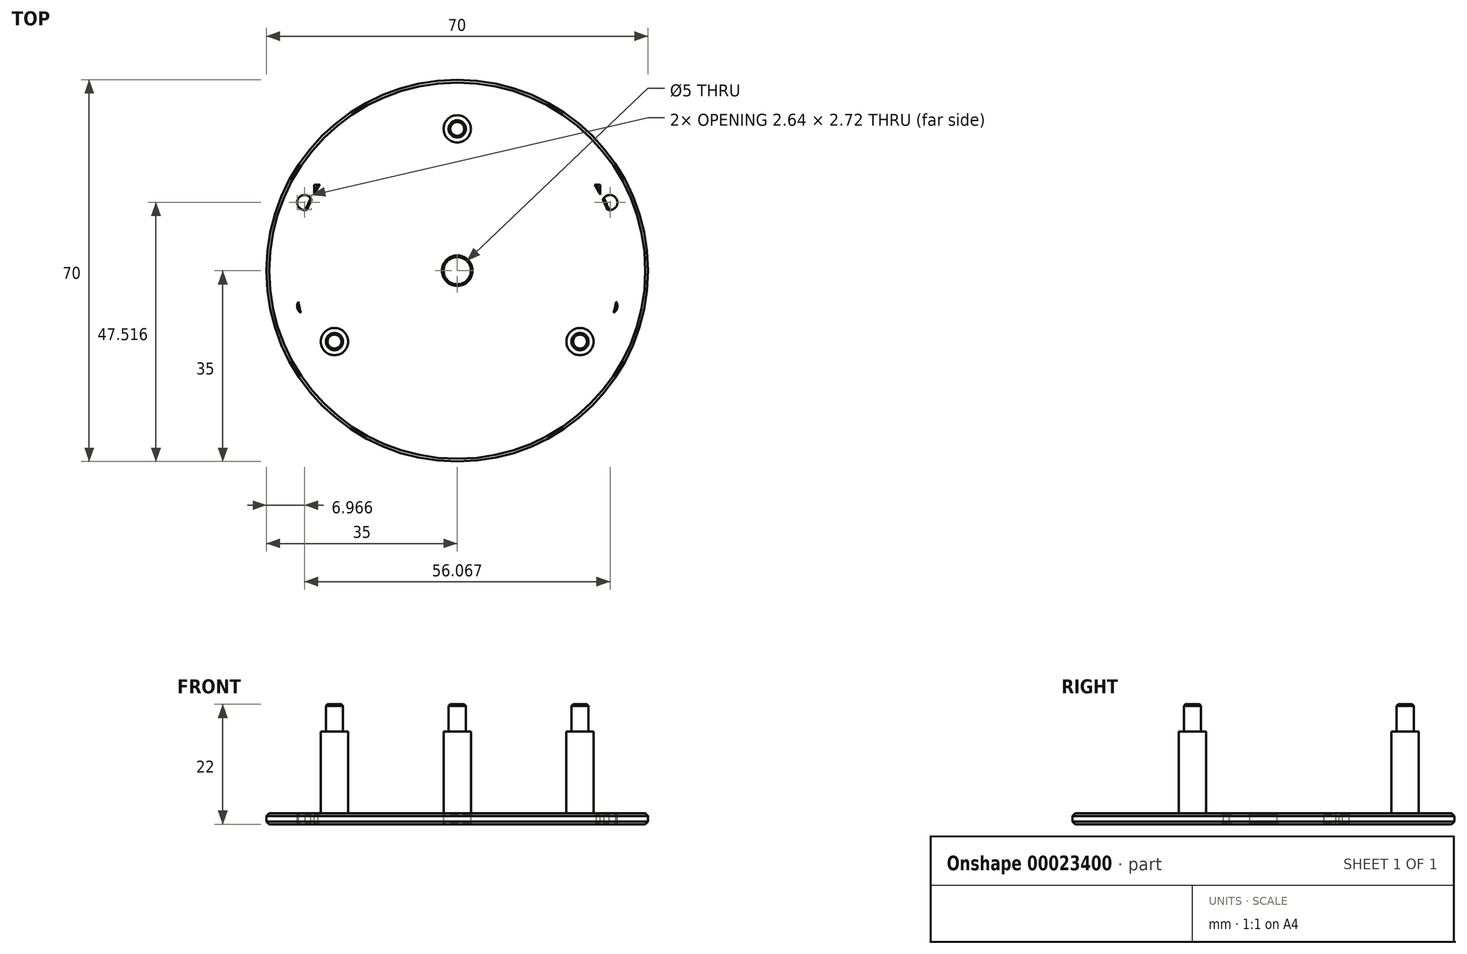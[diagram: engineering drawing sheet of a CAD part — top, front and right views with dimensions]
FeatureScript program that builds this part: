
annotation { "Feature Type Name" : "Feature", "Feature Type Description" : "" }
export const myFeature = defineFeature(function(context is Context, id is Id, definition is map)
    precondition{}
    {
        {
            var Q0;
            Q0=qCreatedBy(makeId("Top.planeOp"),FACE);
            var sketch = newSketch(context, id + "F0", { "sketchPlane" : qUnion([Q0])});
            skCircle(sketch, "E0", {"center": v(0, 0) * mm, "radius": 35 * mm});
            skCircle(sketch, "E1", {"center": v(0, 0) * mm, "radius": 30 * mm, "construction": true});
            skCircle(sketch, "E2.cCircle", {"center": v(0, 0) * mm, "radius": 26 * mm, "construction": true});
            skLineSegment(sketch, "E2.0", {"start": v(0, 26) * mm, "end": v(22.52, -13) * mm, "construction": true});
            skLineSegment(sketch, "E2.1", {"start": v(22.52, -13) * mm, "end": v(-22.52, -13) * mm, "construction": true});
            skLineSegment(sketch, "E2.2", {"start": v(-22.52, -13) * mm, "end": v(0, 26) * mm, "construction": true});
            skCircle(sketch, "E3", {"center": v(0, 26) * mm, "radius": 1.57 * mm});
            skCircle(sketch, "E4", {"center": v(22.52, -13) * mm, "radius": 1.57 * mm});
            skCircle(sketch, "E5", {"center": v(-22.52, -13) * mm, "radius": 1.57 * mm});
            skSolve(sketch);
        }
        {
            var Q0;
            Q0=makeQuery(id+"F0.imprint","IMPRINT",FACE,{"disambiguationData":[TD([[makeQuery(id+"F0.imprint","IMPRINT",EDGE,{"derivedFrom":sQuery(id+"F0.wireOp",EDGE,"E0")}),1.0]])]});
            extrude(context, id + "F1", {"entities" : qUnion([Q0]), "oppositeDirection" : true, "depth" : 2 * mm});
        }
        {
            var Q0;
            Q0=makeQuery(id+"F1.opExtrude","CAP_FACE",FACE,{"disambiguationData":[OSD([sQuery(id+"F0.wireOp",EDGE,"E0"),sQuery(id+"F0.wireOp",EDGE,"E3"),sQuery(id+"F0.wireOp",EDGE,"E4"),sQuery(id+"F0.wireOp",EDGE,"E5")])],"isStart":true});
            var sketch = newSketch(context, id + "F2", { "sketchPlane" : qUnion([Q0])});
            skLineSegment(sketch, "E6.bottom", {"start": v(-31.25, 15.75) * mm, "end": v(31.25, 15.75) * mm, "construction": true});
            skLineSegment(sketch, "E6.top", {"start": v(-31.25, -9.75) * mm, "end": v(31.25, -9.75) * mm, "construction": true});
            skLineSegment(sketch, "E6.left", {"start": v(-31.25, 15.75) * mm, "end": v(-31.25, -9.75) * mm, "construction": true});
            skLineSegment(sketch, "E6.right", {"start": v(31.25, 15.75) * mm, "end": v(31.25, -9.75) * mm, "construction": true});
            skCircle(sketch, "E7", {"center": v(-28, 12.5) * mm, "radius": 1.38 * mm});
            skCircle(sketch, "E8", {"center": v(-28, -6.5) * mm, "radius": 1.38 * mm});
            skCircle(sketch, "E9", {"center": v(28, 12.5) * mm, "radius": 1.38 * mm});
            skCircle(sketch, "E10", {"center": v(28, -6.5) * mm, "radius": 1.38 * mm});
            skLineSegment(sketch, "E11.bottom", {"start": v(-26.25, 15.75) * mm, "end": v(26.25, 15.75) * mm});
            skLineSegment(sketch, "E11.top", {"start": v(-26.25, -9.75) * mm, "end": v(26.25, -9.75) * mm});
            skLineSegment(sketch, "E11.left", {"start": v(-26.25, 15.75) * mm, "end": v(-26.25, -9.75) * mm});
            skLineSegment(sketch, "E11.right", {"start": v(26.25, 15.75) * mm, "end": v(26.25, -9.75) * mm});
            skPoint(sketch, "E12.0", {"position": v(-22.52, -13) * mm});
            skLineSegment(sketch, "E13", {"start": v(-26.25, 0) * mm, "end": v(26.25, 0) * mm, "construction": true});
            skPoint(sketch, "E14.0", {"position": v(0, 0) * mm});
            skSolve(sketch);
        }
        {
            var Q0;
            Q0=makeQuery(id+"F2.imprint","IMPRINT",FACE,{"disambiguationData":[TD([[makeQuery(id+"F2.imprint","IMPRINT",EDGE,{"derivedFrom":sQuery(id+"F2.wireOp",EDGE,"E7")}),1.0]])]});
            var Q1;
            Q1=makeQuery(id+"F2.imprint","IMPRINT",FACE,{"disambiguationData":[TD([[makeQuery(id+"F2.imprint","IMPRINT",EDGE,{"derivedFrom":sQuery(id+"F2.wireOp",EDGE,"E11.bottom")}),-1.0]])]});
            var Q2;
            Q2=makeQuery(id+"F2.imprint","IMPRINT",FACE,{"disambiguationData":[TD([[makeQuery(id+"F2.imprint","IMPRINT",EDGE,{"derivedFrom":sQuery(id+"F2.wireOp",EDGE,"E8")}),1.0]])]});
            var Q3;
            Q3=makeQuery(id+"F2.imprint","IMPRINT",FACE,{"disambiguationData":[TD([[makeQuery(id+"F2.imprint","IMPRINT",EDGE,{"derivedFrom":sQuery(id+"F2.wireOp",EDGE,"E9")}),1.0]])]});
            var Q4;
            Q4=makeQuery(id+"F2.imprint","IMPRINT",FACE,{"disambiguationData":[TD([[makeQuery(id+"F2.imprint","IMPRINT",EDGE,{"derivedFrom":sQuery(id+"F2.wireOp",EDGE,"E10")}),1.0]])]});
            extrude(context, id + "F3", {"entities" : qUnion([Q0, Q1, Q2, Q3, Q4]), "operationType" : NewBodyOperationType.REMOVE, "endBound" : BoundingType.UP_TO_NEXT, "oppositeDirection" : true, "depth" : 25 * mm});
        }
        {
            var Q0;
            Q0=makeQuery(id+"F1.opExtrude","CAP_EDGE",EDGE,{"disambiguationData":[OSD([sQuery(id+"F0.wireOp",EDGE,"E0")])],"isStart":true});
            var Q1;
            Q1=makeQuery(id+"F1.opExtrude","CAP_EDGE",EDGE,{"disambiguationData":[OSD([sQuery(id+"F0.wireOp",EDGE,"E3")])],"isStart":true});
            var Q2;
            Q2=makeQuery(id+"F1.opExtrude","CAP_EDGE",EDGE,{"disambiguationData":[OSD([sQuery(id+"F0.wireOp",EDGE,"E5")])],"isStart":true});
            var Q3;
            Q3=makeQuery(id+"F1.opExtrude","CAP_EDGE",EDGE,{"disambiguationData":[OSD([sQuery(id+"F0.wireOp",EDGE,"E4")])],"isStart":true});
            var Q4;
            Q4=makeQuery(id+"F1.opExtrude","CAP_EDGE",EDGE,{"disambiguationData":[OSD([sQuery(id+"F0.wireOp",EDGE,"E0")])],"isStart":false});
            var Q5;
            Q5=makeQuery(id+"F1.opExtrude","CAP_EDGE",EDGE,{"disambiguationData":[OSD([sQuery(id+"F0.wireOp",EDGE,"E4")])],"isStart":false});
            var Q6;
            Q6=makeQuery(id+"F1.opExtrude","CAP_EDGE",EDGE,{"disambiguationData":[OSD([sQuery(id+"F0.wireOp",EDGE,"E3")])],"isStart":false});
            var Q7;
            Q7=makeQuery(id+"F1.opExtrude","CAP_EDGE",EDGE,{"disambiguationData":[OSD([sQuery(id+"F0.wireOp",EDGE,"E5")])],"isStart":false});
            var Q8;
            Q8=makeQuery(id+"F3.boolean.opBoolean","COPY",EDGE,{"derivedFrom":makeQuery(id+"F3.opExtrude","CAP_EDGE",EDGE,{"disambiguationData":[OSD([sQuery(id+"F2.wireOp",EDGE,"E7")])],"isStart":true})});
            var Q9;
            Q9=makeQuery(id+"F3.boolean.opBoolean","COPY",EDGE,{"derivedFrom":makeQuery(id+"F3.opExtrude","CAP_EDGE",EDGE,{"disambiguationData":[OSD([sQuery(id+"F2.wireOp",EDGE,"E8")])],"isStart":true})});
            var Q10;
            Q10=makeQuery(id+"F3.boolean.opBoolean","COPY",EDGE,{"derivedFrom":makeQuery(id+"F3.opExtrude","CAP_EDGE",EDGE,{"disambiguationData":[OSD([sQuery(id+"F2.wireOp",EDGE,"E9")])],"isStart":true})});
            var Q11;
            Q11=makeQuery(id+"F3.boolean.opBoolean","COPY",EDGE,{"derivedFrom":makeQuery(id+"F3.opExtrude","CAP_EDGE",EDGE,{"disambiguationData":[OSD([sQuery(id+"F2.wireOp",EDGE,"E10")])],"isStart":true})});
            var Q12;
            Q12=makeQuery(id+"F3.boolean.opBoolean","COPY",EDGE,{"derivedFrom":makeQuery(id+"F3.opExtrude","CAP_EDGE",EDGE,{"disambiguationData":[OSD([sQuery(id+"F2.wireOp",EDGE,"E11.right")])],"isStart":true})});
            var Q13;
            Q13=makeQuery(id+"F3.boolean.opBoolean","COPY",EDGE,{"derivedFrom":makeQuery(id+"F3.opExtrude","CAP_EDGE",EDGE,{"disambiguationData":[OSD([sQuery(id+"F2.wireOp",EDGE,"E11.bottom")])],"isStart":false})});
            var Q14;
            Q14=makeQuery(id+"F3.boolean.opBoolean","COPY",EDGE,{"derivedFrom":makeQuery(id+"F3.opExtrude","CAP_EDGE",EDGE,{"disambiguationData":[OSD([sQuery(id+"F2.wireOp",EDGE,"E11.left")])],"isStart":false})});
            var Q15;
            Q15=makeQuery(id+"F3.boolean.opBoolean","COPY",EDGE,{"derivedFrom":makeQuery(id+"F3.opExtrude","CAP_EDGE",EDGE,{"disambiguationData":[OSD([sQuery(id+"F2.wireOp",EDGE,"E11.top")])],"isStart":false})});
            var Q16;
            Q16=makeQuery(id+"F3.boolean.opBoolean","COPY",EDGE,{"derivedFrom":makeQuery(id+"F3.opExtrude","CAP_EDGE",EDGE,{"disambiguationData":[OSD([sQuery(id+"F2.wireOp",EDGE,"E7")])],"isStart":false})});
            var Q17;
            Q17=makeQuery(id+"F3.boolean.opBoolean","COPY",EDGE,{"derivedFrom":makeQuery(id+"F3.opExtrude","CAP_EDGE",EDGE,{"disambiguationData":[OSD([sQuery(id+"F2.wireOp",EDGE,"E8")])],"isStart":false})});
            var Q18;
            Q18=makeQuery(id+"F3.boolean.opBoolean","COPY",EDGE,{"derivedFrom":makeQuery(id+"F3.opExtrude","CAP_EDGE",EDGE,{"disambiguationData":[OSD([sQuery(id+"F2.wireOp",EDGE,"E9")])],"isStart":false})});
            var Q19;
            Q19=makeQuery(id+"F3.boolean.opBoolean","COPY",EDGE,{"derivedFrom":makeQuery(id+"F3.opExtrude","CAP_EDGE",EDGE,{"disambiguationData":[OSD([sQuery(id+"F2.wireOp",EDGE,"E10")])],"isStart":false})});
            var Q20;
            Q20=makeQuery(id+"F3.boolean.opBoolean","COPY",EDGE,{"derivedFrom":makeQuery(id+"F3.opExtrude","CAP_EDGE",EDGE,{"disambiguationData":[OSD([sQuery(id+"F2.wireOp",EDGE,"E11.right")])],"isStart":false})});
            var Q21;
            Q21=makeQuery(id+"F3.boolean.opBoolean","COPY",EDGE,{"derivedFrom":makeQuery(id+"F3.opExtrude","CAP_EDGE",EDGE,{"disambiguationData":[OSD([sQuery(id+"F2.wireOp",EDGE,"E11.bottom")])],"isStart":true})});
            var Q22;
            Q22=makeQuery(id+"F3.boolean.opBoolean","COPY",EDGE,{"derivedFrom":makeQuery(id+"F3.opExtrude","CAP_EDGE",EDGE,{"disambiguationData":[OSD([sQuery(id+"F2.wireOp",EDGE,"E11.left")])],"isStart":true})});
            var Q23;
            Q23=makeQuery(id+"F3.boolean.opBoolean","COPY",EDGE,{"derivedFrom":makeQuery(id+"F3.opExtrude","CAP_EDGE",EDGE,{"disambiguationData":[OSD([sQuery(id+"F2.wireOp",EDGE,"E11.top")])],"isStart":true})});
            chamfer(context, id + "F4", {"entities" : qUnion([Q0, Q1, Q2, Q3, Q4, Q5, Q6, Q7, Q8, Q9, Q10, Q11, Q12, Q13, Q14, Q15, Q16, Q17, Q18, Q19, Q20, Q21, Q22, Q23]), "width" : .5 * mm, "tangentPropagation" : true});
        }
        {
            var Q0;
            Q0=makeQuery(id+"F0.imprint","IMPRINT",FACE,{"disambiguationData":[TD([[makeQuery(id+"F0.imprint","IMPRINT",EDGE,{"derivedFrom":sQuery(id+"F0.wireOp",EDGE,"E0")}),1.0]])]});
            var sketch = newSketch(context, id + "F5", { "sketchPlane" : qUnion([Q0])});
            skCircle(sketch, "E15.0", {"center": v(0, 0) * mm, "radius": 30 * mm});
            skPoint(sketch, "E16.0", {"position": v(0, 26) * mm});
            skPoint(sketch, "E17.0", {"position": v(-22.52, -13) * mm});
            skPoint(sketch, "E18.0", {"position": v(22.52, -13) * mm});
            skCircle(sketch, "E19.0", {"center": v(0, 26) * mm, "radius": 1.57 * mm});
            skCircle(sketch, "E20.0", {"center": v(-22.52, -13) * mm, "radius": 1.57 * mm});
            skCircle(sketch, "E21.0", {"center": v(22.52, -13) * mm, "radius": 1.57 * mm});
            skCircle(sketch, "E22", {"center": v(0, 0) * mm, "radius": 2.5 * mm});
            skCircle(sketch, "E23", {"center": v(0, 26) * mm, "radius": 2.5 * mm});
            skCircle(sketch, "E24", {"center": v(22.52, -13) * mm, "radius": 2.5 * mm});
            skCircle(sketch, "E25", {"center": v(-22.52, -13) * mm, "radius": 2.5 * mm});
            skSolve(sketch);
        }
        {
            var Q0;
            Q0=makeQuery(id+"F5.imprint","IMPRINT",FACE,{"disambiguationData":[TD([[makeQuery(id+"F5.imprint","IMPRINT",EDGE,{"derivedFrom":sQuery(id+"F5.wireOp",EDGE,"E15.0")}),1.0]])]});
            var Q1;
            Q1=makeQuery(id+"F5.imprint","IMPRINT",FACE,{"disambiguationData":[TD([[makeQuery(id+"F5.imprint","IMPRINT",EDGE,{"derivedFrom":sQuery(id+"F5.wireOp",EDGE,"E20.0")}),1.0]])]});
            var Q2;
            Q2=makeQuery(id+"F5.imprint","IMPRINT",FACE,{"disambiguationData":[TD([[makeQuery(id+"F5.imprint","IMPRINT",EDGE,{"derivedFrom":sQuery(id+"F5.wireOp",EDGE,"E21.0")}),1.0]])]});
            var Q3;
            Q3=makeQuery(id+"F5.imprint","IMPRINT",FACE,{"disambiguationData":[TD([[makeQuery(id+"F5.imprint","IMPRINT",EDGE,{"derivedFrom":sQuery(id+"F5.wireOp",EDGE,"E19.0")}),1.0]])]});
            var Q4;
            Q4=makeQuery(id+"F5.imprint","IMPRINT",FACE,{"disambiguationData":[TD([[makeQuery(id+"F5.imprint","IMPRINT",EDGE,{"derivedFrom":sQuery(id+"F5.wireOp",EDGE,"E19.0")}),-1.0]])]});
            var Q5;
            Q5=makeQuery(id+"F5.imprint","IMPRINT",FACE,{"disambiguationData":[TD([[makeQuery(id+"F5.imprint","IMPRINT",EDGE,{"derivedFrom":sQuery(id+"F5.wireOp",EDGE,"E20.0")}),-1.0]])]});
            var Q6;
            Q6=makeQuery(id+"F5.imprint","IMPRINT",FACE,{"disambiguationData":[TD([[makeQuery(id+"F5.imprint","IMPRINT",EDGE,{"derivedFrom":sQuery(id+"F5.wireOp",EDGE,"E21.0")}),-1.0]])]});
            extrude(context, id + "F6", {"entities" : qUnion([Q0, Q1, Q2, Q3, Q4, Q5, Q6]), "oppositeDirection" : true, "depth" : 2 * mm});
        }
        {
            var Q0;
            Q0=makeQuery(id+"F5.imprint","IMPRINT",FACE,{"disambiguationData":[TD([[makeQuery(id+"F5.imprint","IMPRINT",EDGE,{"derivedFrom":sQuery(id+"F5.wireOp",EDGE,"E19.0")}),1.0]])]});
            var Q1;
            Q1=makeQuery(id+"F5.imprint","IMPRINT",FACE,{"disambiguationData":[TD([[makeQuery(id+"F5.imprint","IMPRINT",EDGE,{"derivedFrom":sQuery(id+"F5.wireOp",EDGE,"E20.0")}),1.0]])]});
            var Q2;
            Q2=makeQuery(id+"F5.imprint","IMPRINT",FACE,{"disambiguationData":[TD([[makeQuery(id+"F5.imprint","IMPRINT",EDGE,{"derivedFrom":sQuery(id+"F5.wireOp",EDGE,"E21.0")}),1.0]])]});
            extrude(context, id + "F7", {"entities" : qUnion([Q0, Q1, Q2]), "operationType" : NewBodyOperationType.ADD, "depth" : 20 * mm});
        }
        {
            var Q0;
            Q0=makeQuery(id+"F5.imprint","IMPRINT",FACE,{"disambiguationData":[TD([[makeQuery(id+"F5.imprint","IMPRINT",EDGE,{"derivedFrom":sQuery(id+"F5.wireOp",EDGE,"E19.0")}),-1.0]])]});
            var Q1;
            Q1=makeQuery(id+"F5.imprint","IMPRINT",FACE,{"disambiguationData":[TD([[makeQuery(id+"F5.imprint","IMPRINT",EDGE,{"derivedFrom":sQuery(id+"F5.wireOp",EDGE,"E20.0")}),-1.0]])]});
            var Q2;
            Q2=makeQuery(id+"F5.imprint","IMPRINT",FACE,{"disambiguationData":[TD([[makeQuery(id+"F5.imprint","IMPRINT",EDGE,{"derivedFrom":sQuery(id+"F5.wireOp",EDGE,"E21.0")}),-1.0]])]});
            extrude(context, id + "F8", {"entities" : qUnion([Q0, Q1, Q2]), "operationType" : NewBodyOperationType.ADD, "depth" : 15 * mm});
        }
        {
            var Q0;
            Q0=makeQuery(id+"F7.opExtrude","CAP_EDGE",EDGE,{"disambiguationData":[OSD([sQuery(id+"F5.wireOp",EDGE,"E21.0")])],"isStart":false});
            var Q1;
            Q1=makeQuery(id+"F7.opExtrude","CAP_EDGE",EDGE,{"disambiguationData":[OSD([sQuery(id+"F5.wireOp",EDGE,"E20.0")])],"isStart":false});
            var Q2;
            Q2=makeQuery(id+"F7.opExtrude","CAP_EDGE",EDGE,{"disambiguationData":[OSD([sQuery(id+"F5.wireOp",EDGE,"E19.0")])],"isStart":false});
            var Q3;
            Q3=makeQuery(id+"F6.opExtrude","CAP_EDGE",EDGE,{"disambiguationData":[OSD([sQuery(id+"F5.wireOp",EDGE,"E22")])],"isStart":true});
            var Q4;
            Q4=makeQuery(id+"F6.opExtrude","CAP_EDGE",EDGE,{"disambiguationData":[OSD([sQuery(id+"F5.wireOp",EDGE,"E22")])],"isStart":false});
            var Q5;
            Q5=makeQuery(id+"F6.opExtrude","CAP_EDGE",EDGE,{"disambiguationData":[OSD([sQuery(id+"F5.wireOp",EDGE,"E15.0")])],"isStart":true});
            var Q6;
            Q6=makeQuery(id+"F6.opExtrude","CAP_EDGE",EDGE,{"disambiguationData":[OSD([sQuery(id+"F5.wireOp",EDGE,"E15.0")])],"isStart":false});
            chamfer(context, id + "F9", {"entities" : qUnion([Q0, Q1, Q2, Q3, Q4, Q5, Q6]), "width" : .3 * mm, "tangentPropagation" : true});
        }
    });
